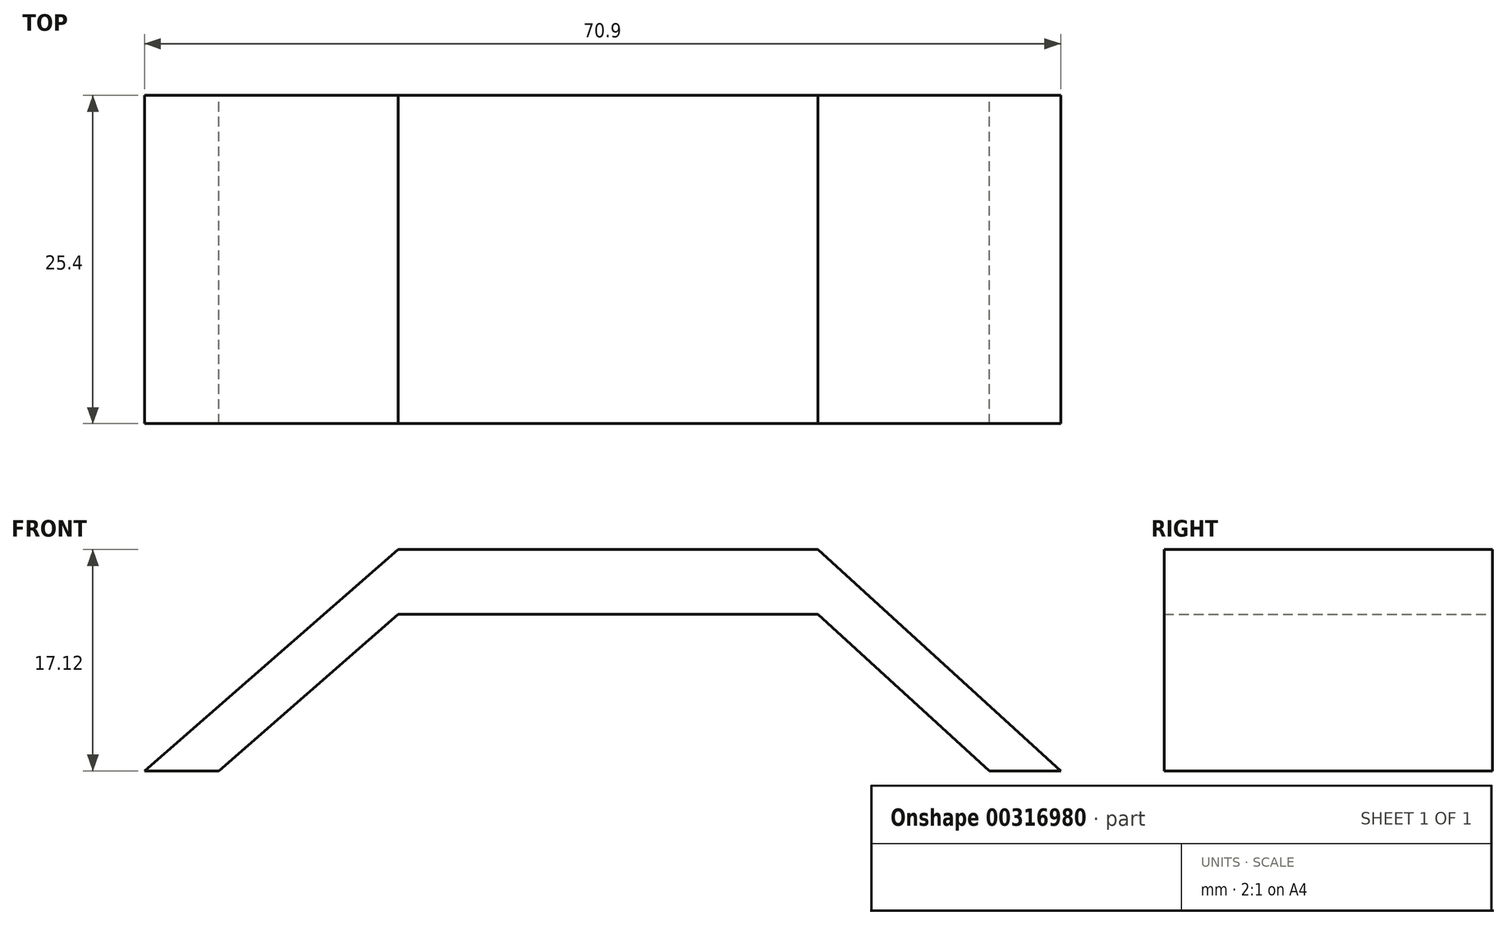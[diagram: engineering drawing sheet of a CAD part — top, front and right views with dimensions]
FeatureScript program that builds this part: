
annotation { "Feature Type Name" : "Feature", "Feature Type Description" : "" }
export const myFeature = defineFeature(function(context is Context, id is Id, definition is map)
    precondition{}
    {
        {
            var Q0;
            Q0=qCreatedBy(makeId("Front.planeOp"),FACE);
            var sketch = newSketch(context, id + "F0", { "sketchPlane" : qUnion([Q0])});
            skLineSegment(sketch, "E0", {"start": v(-42.36, 0) * mm, "end": v(-22.73, 17.12) * mm});
            skLineSegment(sketch, "E1", {"start": v(-22.73, 17.12) * mm, "end": v(9.74, 17.12) * mm});
            skLineSegment(sketch, "E2", {"start": v(9.74, 17.12) * mm, "end": v(28.54, 0) * mm});
            skLineSegment(sketch, "E3", {"start": v(-42.36, 0) * mm, "end": v(-29.23, 0) * mm});
            skLineSegment(sketch, "E4", {"start": v(-22.73, 12.1) * mm, "end": v(-36.6, 0) * mm});
            skLineSegment(sketch, "E5", {"start": v(-22.73, 12.1) * mm, "end": v(9.74, 12.1) * mm});
            skLineSegment(sketch, "E6", {"start": v(9.74, 12.1) * mm, "end": v(23.03, 0) * mm});
            skLineSegment(sketch, "E7", {"start": v(23.03, 0) * mm, "end": v(28.54, 0) * mm});
            skSolve(sketch);
        }
        {
            var Q0;
            {var subQ1=sQuery(id+"F0.wireOp",EDGE,"E0");Q0=makeQuery(id+"F0.imprint","IMPRINT",FACE,{"disambiguationData":[TD([[makeQuery(id+"F0.imprint","IMPRINT",EDGE,{"derivedFrom":subQ1}),-1.0]])]});}
            extrude(context, id + "F1", {"entities" : qUnion([Q0]), "depth" : 25.4 * mm});
        }
    });
